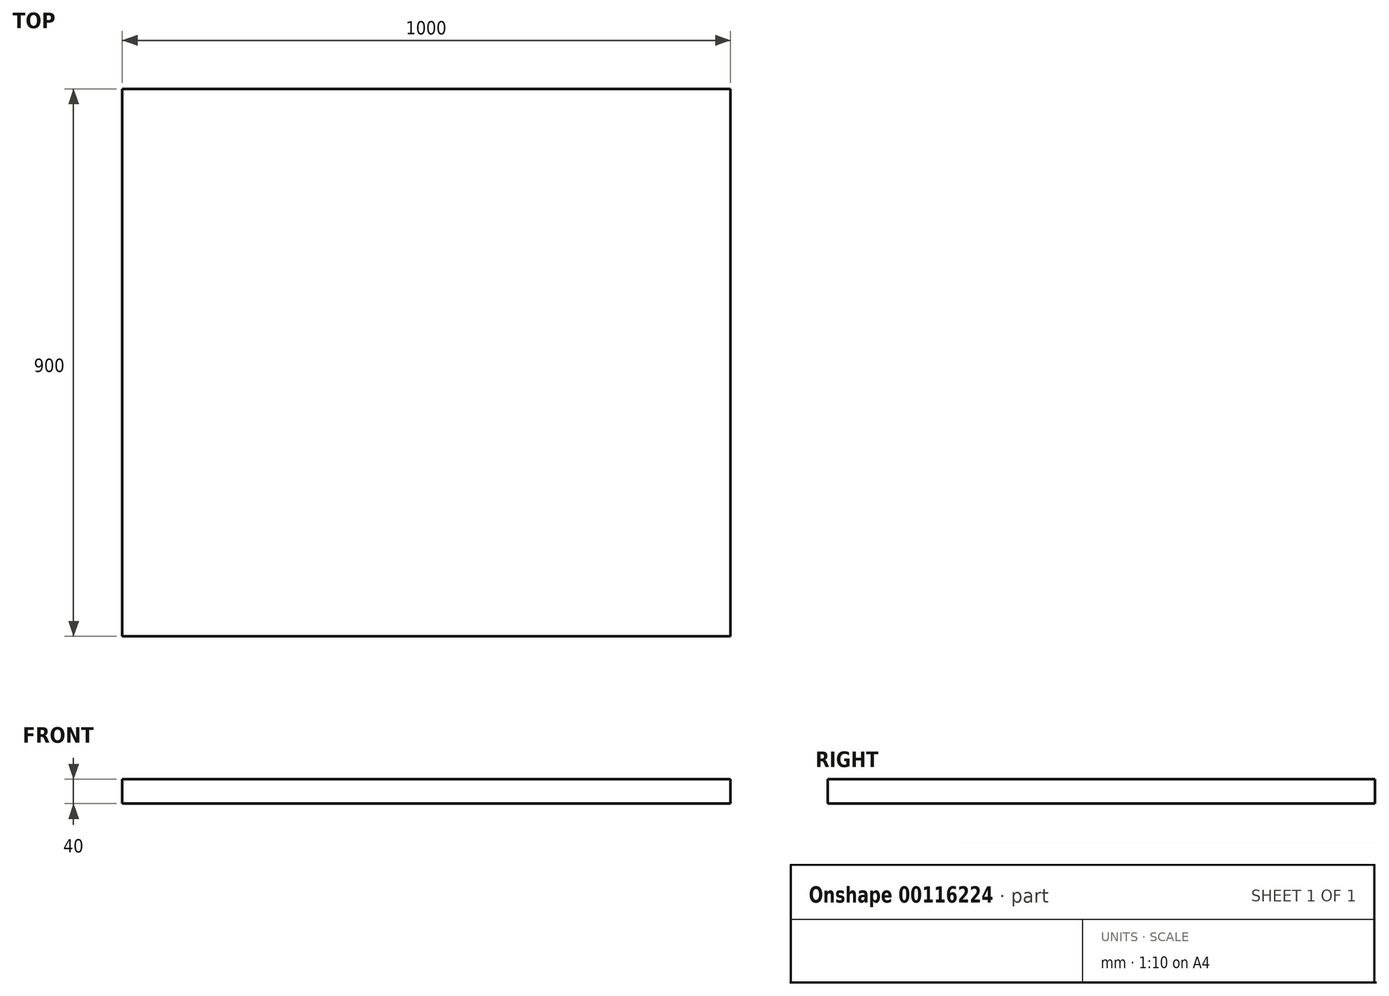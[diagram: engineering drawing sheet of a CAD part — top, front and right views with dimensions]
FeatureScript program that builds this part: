
annotation { "Feature Type Name" : "Feature", "Feature Type Description" : "" }
export const myFeature = defineFeature(function(context is Context, id is Id, definition is map)
    precondition{}
    {
        {
            var Q0;
            Q0=qCreatedBy(makeId("Top.planeOp"),FACE);
            var sketch = newSketch(context, id + "F0", { "sketchPlane" : qUnion([Q0])});
            skLineSegment(sketch, "E0.bottom", {"start": v(0, 0) * mm, "end": v(1000, 0) * mm});
            skLineSegment(sketch, "E0.top", {"start": v(0, 900) * mm, "end": v(1000, 900) * mm});
            skLineSegment(sketch, "E0.left", {"start": v(0, 0) * mm, "end": v(0, 900) * mm});
            skLineSegment(sketch, "E0.right", {"start": v(1000, 0) * mm, "end": v(1000, 900) * mm});
            skSolve(sketch);
        }
        {
            var Q0;
            Q0=makeQuery(id+"F0.imprint","IMPRINT",FACE,{"disambiguationData":[TD([[makeQuery(id+"F0.imprint","IMPRINT",EDGE,{"derivedFrom":sQuery(id+"F0.wireOp",EDGE,"E0.bottom")}),1.0]])]});
            extrude(context, id + "F1", {"entities" : qUnion([Q0]), "depth" : 40 * mm});
        }
    });
